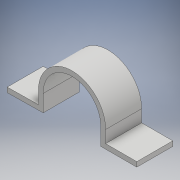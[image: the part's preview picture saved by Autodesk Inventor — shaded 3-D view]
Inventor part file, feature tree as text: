
AUTODESK INVENTOR PART (.ipt)
format: ipt  version: 2017 (Build 210142000, 142)  size: 115,200 bytes
history: native  units: mm
features: extrude x1, sketch x1
ambient origin geometry x8: Origin, YZ Plane, XZ Plane, XY Plane, X Axis, Y Axis, Z Axis, Center Point
bodies: Body1 (feature_tree)
feature tree (2):
  extrude  "Extrusion3"  Depth=2.0mm
  sketch  "Sketch3"  dims[d23=15.0mm d24=0.0mm d25=24.0mm d26=7.0mm d27=15.0mm d28=15.0mm d29=2.0mm]
